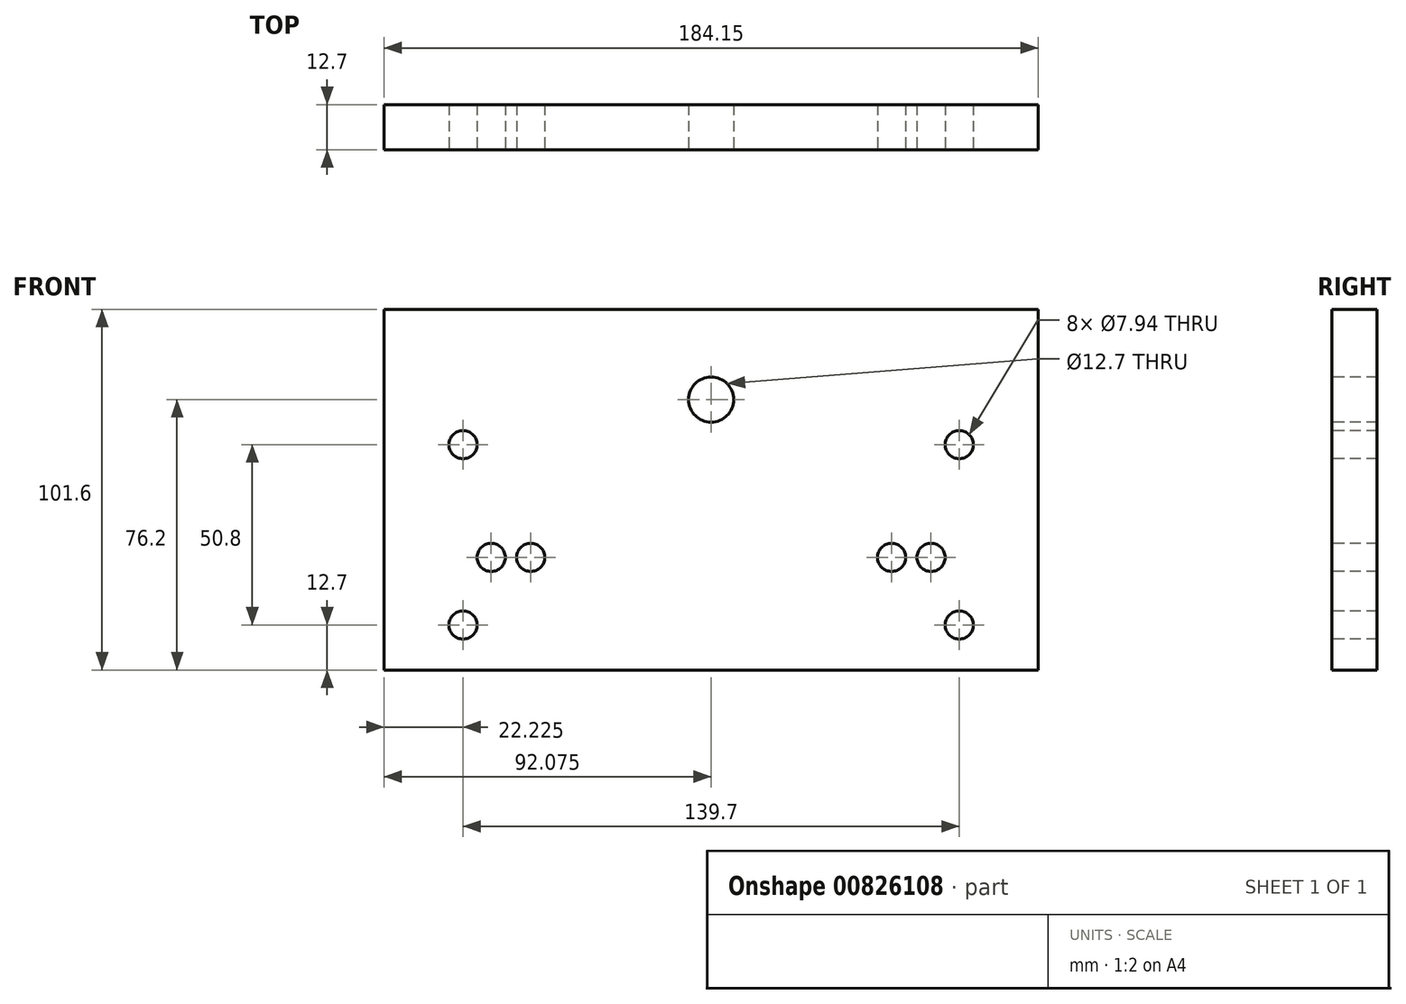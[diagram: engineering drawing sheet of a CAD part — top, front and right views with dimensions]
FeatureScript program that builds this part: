
annotation { "Feature Type Name" : "Feature", "Feature Type Description" : "" }
export const myFeature = defineFeature(function(context is Context, id is Id, definition is map)
    precondition{}
    {
        {
            var Q0;
            Q0=qCreatedBy(makeId("Front.planeOp"),FACE);
            var sketch = newSketch(context, id + "F0", { "sketchPlane" : qUnion([Q0])});
            skLineSegment(sketch, "E0.bottom", {"start": v(0, 0) * mm, "end": v(184.15, 0) * mm});
            skLineSegment(sketch, "E0.top", {"start": v(0, 101.6) * mm, "end": v(184.15, 101.6) * mm});
            skLineSegment(sketch, "E0.left", {"start": v(0, 0) * mm, "end": v(0, 101.6) * mm});
            skLineSegment(sketch, "E0.right", {"start": v(184.15, 0) * mm, "end": v(184.15, 101.6) * mm});
            skSolve(sketch);
        }
        {
            var Q0;
            Q0=qSketchRegion(id+"F0",true);
            extrude(context, id + "F1", {"entities" : qUnion([Q0]), "depth" : 12.7 * mm, "offsetDistance" : 25.4 * mm});
        }
        {
            var Q0;
            Q0=makeQuery(id+"F1.opExtrude","CAP_FACE",FACE,{"disambiguationData":[OSD([sQuery(id+"F0.wireOp",EDGE,"E0.bottom"),sQuery(id+"F0.wireOp",EDGE,"E0.top"),sQuery(id+"F0.wireOp",EDGE,"E0.left"),sQuery(id+"F0.wireOp",EDGE,"E0.right")])],"isStart":false});
            var sketch = newSketch(context, id + "F2", { "sketchPlane" : qUnion([Q0])});
            skPoint(sketch, "E1", {"position": v(92.08, 76.2) * mm});
            skSolve(sketch);
        }
        {
            var Q0;
            Q0=sQuery(id+"F2.wireOp",VERTEX,"E1");
            var Q1;
            Q1=makeQuery(id+"F1.opExtrude","SWEPT_BODY",BODY,{"disambiguationData":[OSD([sQuery(id+"F0.wireOp",EDGE,"E0.bottom"),sQuery(id+"F0.wireOp",EDGE,"E0.top"),sQuery(id+"F0.wireOp",EDGE,"E0.left"),sQuery(id+"F0.wireOp",EDGE,"E0.right")])]});
            hole(context, id + "F3", {"style" : HoleStyle.SIMPLE, "endStyle" : HoleEndStyle.THROUGH, "holeDiameter" : 12.7 * mm, "majorDiameter" : 6.35 * mm, "isTappedThrough" : true, "tappedDepth" : 12.7 * mm, "tapClearance" : 3, "locations" : qUnion([Q0]), "scope" : qUnion([Q1])});
        }
        {
            var Q0;
            Q0=makeQuery(id+"F1.opExtrude","CAP_FACE",FACE,{"disambiguationData":[OSD([sQuery(id+"F0.wireOp",EDGE,"E0.bottom"),sQuery(id+"F0.wireOp",EDGE,"E0.top"),sQuery(id+"F0.wireOp",EDGE,"E0.left"),sQuery(id+"F0.wireOp",EDGE,"E0.right")])],"isStart":false});
            var sketch = newSketch(context, id + "F4", { "sketchPlane" : qUnion([Q0])});
            skPoint(sketch, "E2", {"position": v(161.93, 63.5) * mm});
            skPoint(sketch, "E3", {"position": v(22.23, 63.5) * mm});
            skPoint(sketch, "E4", {"position": v(197.63, -129.05) * mm});
            skLineSegment(sketch, "E5", {"start": v(92.08, 76.2) * mm, "end": v(92.08, 0) * mm, "construction": true});
            skPoint(sketch, "E6", {"position": v(22.23, 12.7) * mm});
            skPoint(sketch, "E7", {"position": v(161.92, 12.7) * mm});
            skSolve(sketch);
        }
        {
            var Q0;
            Q0=sQuery(id+"F4.wireOp",VERTEX,"E3");
            var Q1;
            Q1=sQuery(id+"F4.wireOp",VERTEX,"E2");
            var Q2;
            Q2=sQuery(id+"F4.wireOp",VERTEX,"E7");
            var Q3;
            Q3=sQuery(id+"F4.wireOp",VERTEX,"E6");
            var Q4;
            Q4=makeQuery(id+"F1.opExtrude","SWEPT_BODY",BODY,{"disambiguationData":[OSD([sQuery(id+"F0.wireOp",EDGE,"E0.bottom"),sQuery(id+"F0.wireOp",EDGE,"E0.top"),sQuery(id+"F0.wireOp",EDGE,"E0.left"),sQuery(id+"F0.wireOp",EDGE,"E0.right")])]});
            hole(context, id + "F5", {"style" : HoleStyle.SIMPLE, "endStyle" : HoleEndStyle.THROUGH, "holeDiameter" : 7.94 * mm, "majorDiameter" : 6.35 * mm, "isTappedThrough" : true, "tappedDepth" : 12.7 * mm, "tapClearance" : 3, "locations" : qUnion([Q0, Q1, Q2, Q3]), "scope" : qUnion([Q4])});
        }
        {
            var Q0;
            Q0=makeQuery(id+"F1.opExtrude","CAP_FACE",FACE,{"disambiguationData":[OSD([sQuery(id+"F0.wireOp",EDGE,"E0.bottom"),sQuery(id+"F0.wireOp",EDGE,"E0.top"),sQuery(id+"F0.wireOp",EDGE,"E0.left"),sQuery(id+"F0.wireOp",EDGE,"E0.right")])],"isStart":false});
            var sketch = newSketch(context, id + "F6", { "sketchPlane" : qUnion([Q0])});
            skPoint(sketch, "E8", {"position": v(41.27, 31.75) * mm});
            skPoint(sketch, "E9", {"position": v(142.88, 31.75) * mm});
            skLineSegment(sketch, "E10", {"start": v(92.08, 76.2) * mm, "end": v(92.08, -25.83) * mm, "construction": true});
            skPoint(sketch, "E11", {"position": v(153.99, 31.75) * mm});
            skPoint(sketch, "E12", {"position": v(30.16, 31.75) * mm});
            skSolve(sketch);
        }
        {
            var Q0;
            Q0=sQuery(id+"F6.wireOp",VERTEX,"E8");
            var Q1;
            Q1=sQuery(id+"F6.wireOp",VERTEX,"E9");
            var Q2;
            Q2=sQuery(id+"F6.wireOp",VERTEX,"E12");
            var Q3;
            Q3=sQuery(id+"F6.wireOp",VERTEX,"E11");
            var Q4;
            Q4=makeQuery(id+"F1.opExtrude","SWEPT_BODY",BODY,{"disambiguationData":[OSD([sQuery(id+"F0.wireOp",EDGE,"E0.bottom"),sQuery(id+"F0.wireOp",EDGE,"E0.top"),sQuery(id+"F0.wireOp",EDGE,"E0.left"),sQuery(id+"F0.wireOp",EDGE,"E0.right")])]});
            hole(context, id + "F7", {"style" : HoleStyle.SIMPLE, "endStyle" : HoleEndStyle.THROUGH, "holeDiameter" : 7.94 * mm, "majorDiameter" : 6.35 * mm, "isTappedThrough" : true, "tappedDepth" : 12.7 * mm, "tapClearance" : 3, "locations" : qUnion([Q0, Q1, Q2, Q3]), "scope" : qUnion([Q4])});
        }
    });
